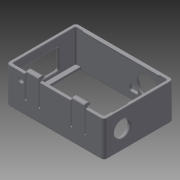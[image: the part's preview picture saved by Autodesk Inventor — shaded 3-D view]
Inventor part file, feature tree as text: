
AUTODESK INVENTOR PART (.ipt)
format: ipt  version: 2015 (Build 190159000, 159)  size: 481,280 bytes
history: native  units: mm
features: fillet x20, sketch x10, extrude x9, hole x4, mirror x2, plane x1
ambient origin geometry x8: Origin, YZ Plane, XZ Plane, XY Plane, X Axis, Y Axis, Z Axis, Center Point
bodies: Solid1 (feature_tree)
feature tree (46):
  sketch  "Sketch1"  dims[d0=60.0mm d1=41.5mm]
  extrude  "Extrusion1"  Depth=41.5mm
  extrude  "Extrusion2"  Depth=3.0mm
  extrude  "Extrusion3"  Depth=2.0mm TaperAngle=0.0deg
  plane  "Work Plane1"
  mirror  "Mirror1"
  extrude  "Extrusion4"  Depth=20.0mm
  extrude  "Extrusion5"  Depth=15.0mm
  mirror  "Mirror2"
  fillet  "Fillet5"  [1 undecoded]
  fillet  "Fillet6"  Radius=1.0mm
  fillet  "Fillet7"  Radius=8.0mm
  extrude  "Extrusion6"  Depth=23.5mm TaperAngle=0.0deg
  fillet  "Fillet8"  Radius=2.0mm
  sketch  "Sketch6"  dims[d19=1.0mm d20=23.5mm d21=0.0mm d22=2.0mm d23=0.0mm]
  hole  "Hole1"  [1 undecoded]
  fillet  "Fillet9"  Radius=2.0mm
  fillet  "Fillet10"  Radius=0.5mm
  hole  "Hole2"  [1 undecoded]
  fillet  "Fillet11"  Radius=50.0mm
  fillet  "Fillet12"  Radius=0.5mm
  extrude  "Extrusion7"  Depth=15.0mm
  fillet  "Fillet13"  Radius=12.5mm
  fillet  "Fillet14"  Radius=1.0mm
  hole  "Hole3"  [1 undecoded]
  fillet  "Fillet15"  Radius=7.0mm
  fillet  "Fillet16"  Radius=7.5mm
  extrude  "Extrusion8"  Depth=0.5mm
  fillet  "Fillet17"  Radius=0.4mm
  hole  "Hole4"  [1 undecoded]
  fillet  "Fillet18"  Radius=2.5mm
  extrude  "Extrusion9"  Depth=2.0mm
  fillet  "Fillet19"  Radius=5.0mm
  fillet  "Fillet20"  Radius=4.0mm
  fillet  "Fillet21"  Radius=1.0mm
  fillet  "Fillet22"  Radius=1.0mm
  fillet  "Fillet23"  Radius=0.5mm
  fillet  "Fillet24"  Radius=12.0mm
  sketch  "Sketch2"  dims[d2=2.0mm d3=3.0mm]
  sketch  "Sketch3"  dims[d4=3.0mm d5=2.0mm d6=0.0mm]
  sketch  "Sketch4"  dims[d7=23.5mm d8=0.0mm d13=20.0mm]
  sketch  "Sketch5"  dims[d14=20.0mm d15=15.0mm d16=90.0deg d17=1.0mm d18=8.0mm]
  sketch  "Sketch7"  dims[d24=2.0mm d25=0.0mm d30=1.0mm d31=2.0mm d32=0.5mm]
  sketch  "Sketch8"  dims[d34=25.0mm d36=1.0mm d37=50.0mm d38=0.5mm d39=0.0mm]
  sketch  "Sketch9"  dims[d40=0.5mm d41=15.0mm d42=12.5mm]
  sketch  "Sketch10"  dims[d43=13.5mm d44=6.0mm d45=4.0mm d46=2.0mm d47=90.0deg d48=2.0mm d49=20.594885mm d50=1.0mm d51=0.5mm d52=7.0mm d53=7.5mm d54=2.5mm d55=6.0mm d56=4.0mm d57=2.0mm d58=90.0deg d59=2.0mm d60=20.594885mm d61=0.5mm d62=0.4mm d64=24.2mm d65=2.5mm d66=2.0mm d67=5.0mm d68=4.0mm d69=1.0mm d70=0.0mm d71=1.0mm d72=0.5mm d73=12.0mm d74=12.0mm d75=10.0mm d76=6.0mm d77=4.0mm d78=2.0mm d79=90.0deg d80=2.0mm d81=20.594885mm d82=1.0mm d83=0.5mm d84=0.5mm d85=0.0mm d86=0.5mm d87=5.0mm d88=9.5mm d89=3.0mm d90=6.0mm d91=4.0mm d92=2.0mm d93=90.0deg d94=2.0mm d95=20.594885mm d96=0.5mm d97=4.0mm d98=7.0mm d99=13.0mm d100=25.0mm d101=2.0mm d102=0.0mm d103=1.0mm d104=1.0mm d105=1.0mm d106=2.0mm d107=0.5mm d108=0.5mm]
note: 5 required parameter values undecoded (feature->parameter linkage not recoverable at this tier; creation-order binding heuristic only, values carry confidence <= 0.55)
